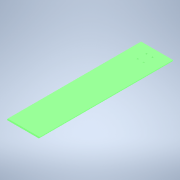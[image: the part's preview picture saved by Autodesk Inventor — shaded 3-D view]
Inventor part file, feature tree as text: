
AUTODESK INVENTOR PART (.ipt)
format: ipt  version: 2022 (Build 260153000, 153)  size: 122,368 bytes
history: native  units: mm
features: sketch x2, other x1, extrude x1, hole x1, chamfer x1
ambient origin geometry x8: Origin, YZ Plane, XZ Plane, XY Plane, X Axis, Y Axis, Z Axis, Center Point
bodies: Body1 (feature_tree)
feature tree (6):
  other  "ソリッド1"
  extrude  "押し出し1"  Depth=336.0mm
  hole  "穴1"  [1 undecoded]
  chamfer  "面取り1"  Distance=2.0mm
  sketch  "スケッチ1"
  sketch  "スケッチ3"
note: 1 required parameter value undecoded (feature->parameter linkage not recoverable at this tier; creation-order binding heuristic only, values carry confidence <= 0.55)
